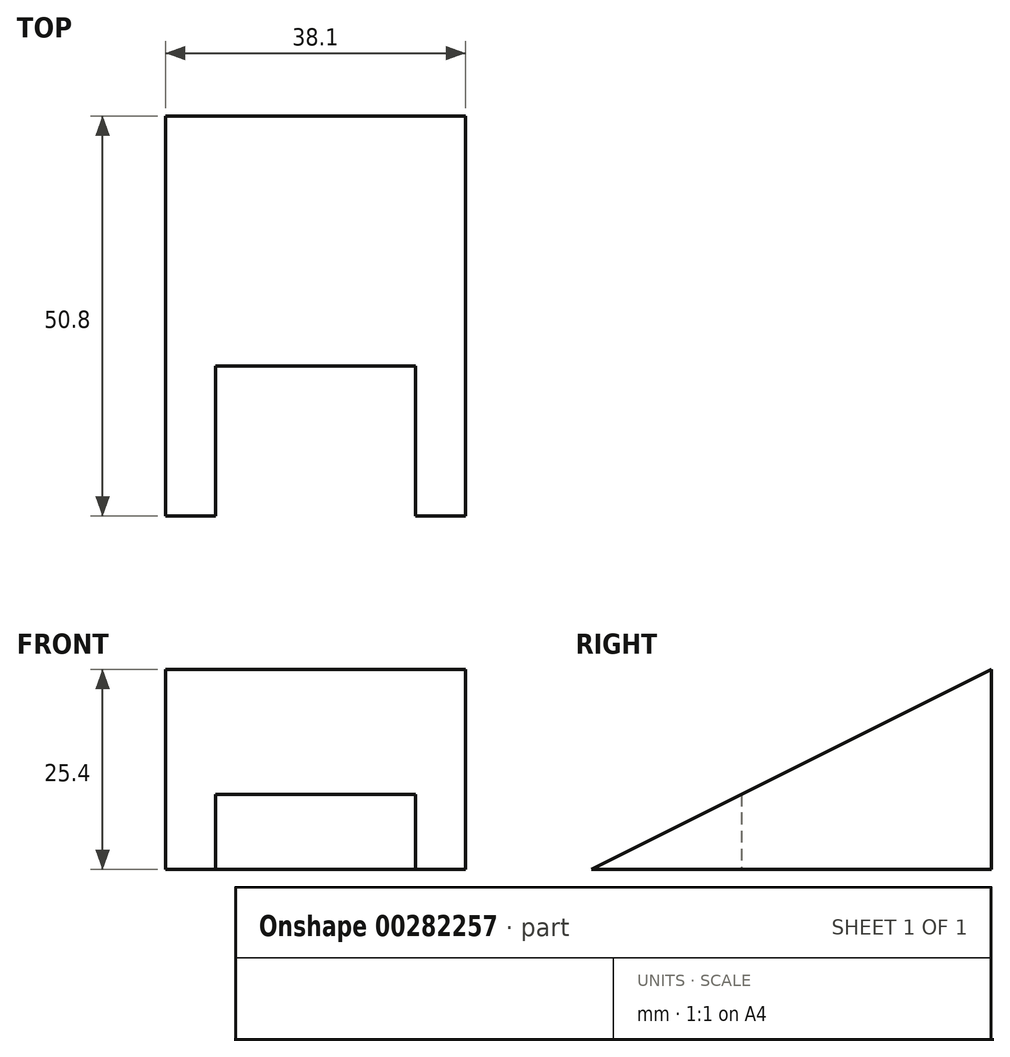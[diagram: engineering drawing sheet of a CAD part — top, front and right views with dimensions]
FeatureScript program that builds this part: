
annotation { "Feature Type Name" : "Feature", "Feature Type Description" : "" }
export const myFeature = defineFeature(function(context is Context, id is Id, definition is map)
    precondition{}
    {
        {
            var Q0;
            Q0=qCreatedBy(makeId("Top.planeOp"),FACE);
            var sketch = newSketch(context, id + "F0", { "sketchPlane" : qUnion([Q0])});
            skLineSegment(sketch, "E0", {"start": v(0, 0) * mm, "end": v(38.1, 0) * mm});
            skLineSegment(sketch, "E1", {"start": v(38.1, 0) * mm, "end": v(38.1, -50.8) * mm});
            skLineSegment(sketch, "E2", {"start": v(0, 0) * mm, "end": v(0, -50.8) * mm});
            skLineSegment(sketch, "E3", {"start": v(0, -50.8) * mm, "end": v(6.35, -50.8) * mm});
            skLineSegment(sketch, "E4", {"start": v(6.35, -50.8) * mm, "end": v(6.35, -31.75) * mm});
            skLineSegment(sketch, "E5", {"start": v(6.35, -31.75) * mm, "end": v(31.75, -31.75) * mm});
            skLineSegment(sketch, "E6", {"start": v(31.75, -31.75) * mm, "end": v(31.75, -50.8) * mm});
            skLineSegment(sketch, "E7", {"start": v(31.75, -50.8) * mm, "end": v(38.1, -50.8) * mm});
            skSolve(sketch);
        }
        {
            var Q0;
            Q0 = qSketchRegion(id + "F0", true);
            extrude(context, id + "F1", {"entities" : qUnion([Q0]), "depth" : 25.4 * mm});
        }
        {
            var Q0;
            Q0=makeQuery(id+"F1.opExtrude","SWEPT_FACE",FACE,{"disambiguationData":[OSD([sQuery(id+"F0.wireOp",EDGE,"E1")])]});
            var sketch = newSketch(context, id + "F2", { "sketchPlane" : qUnion([Q0])});
            skLineSegment(sketch, "E8", {"start": v(-50.8, 0) * mm, "end": v(0, 25.4) * mm});
            skSolve(sketch);
        }
        {
            var Q0;
            Q0=makeQuery(id+"F2.imprint","IMPRINT",FACE,{"disambiguationData":[TD([[makeQuery(id+"F2.imprint","IMPRINT",EDGE,{"derivedFrom":sQuery(id+"F2.wireOp",EDGE,"E8")}),1.0]])]});
            extrude(context, id + "F3", {"entities" : qUnion([Q0]), "operationType" : NewBodyOperationType.REMOVE, "endBound" : BoundingType.THROUGH_ALL, "oppositeDirection" : true, "depth" : 25.4 * mm});
        }
    });
